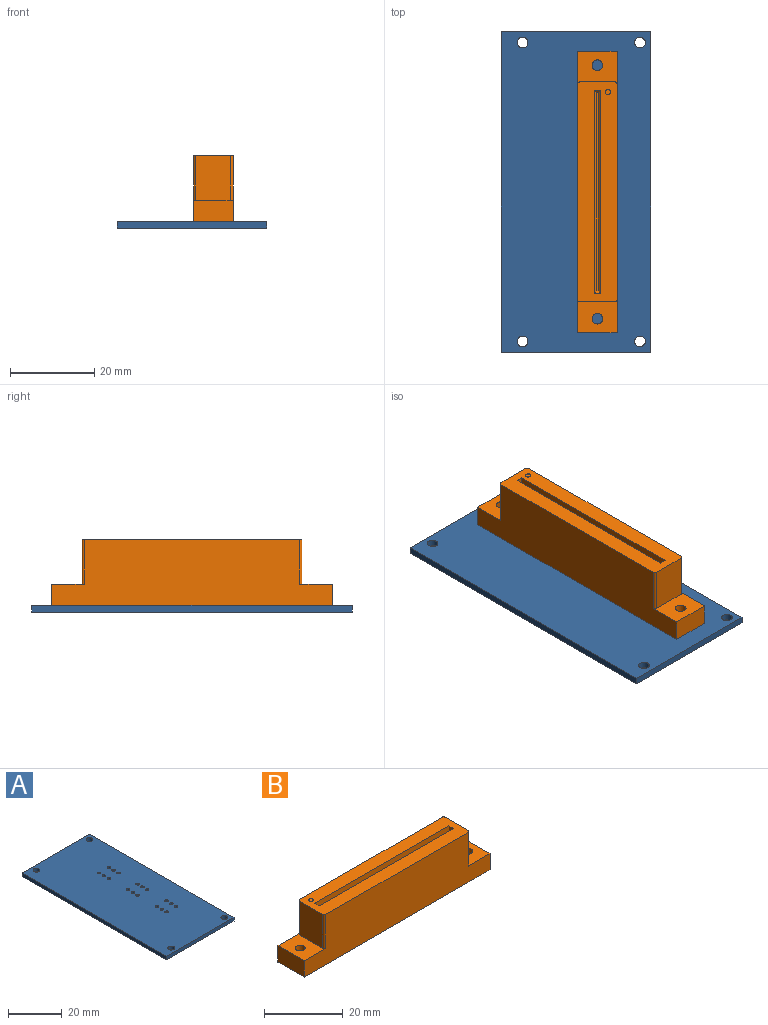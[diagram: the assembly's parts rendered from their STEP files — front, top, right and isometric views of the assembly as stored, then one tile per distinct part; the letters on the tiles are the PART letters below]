
ASSEMBLY  parts=2 mates=1
PART A: 28 faces, bbox 35.6x76.2x1.6 mm
  f0: plane 35.56x1.6mm, normal (0,-1,0), area 56.9mm2, adj f1,f25,f26,f27
  f1: plane 76.2x1.6mm, normal (1,0,0), area 121.9mm2, adj f0,f2,f26,f27
  f2: plane 35.56x1.6mm, normal (0,1,0), area 56.9mm2, adj f1,f25,f26,f27
  f3: cylinder r=0.64mm len=1.6mm, axis (0,0,-1), area 6.4mm2, adj f26,f27
  f4: cylinder r=0.64mm len=1.6mm, axis (0,0,-1), area 6.4mm2, adj f26,f27
  f5: cylinder r=0.64mm len=1.6mm, axis (0,0,-1), area 6.4mm2, adj f26,f27
  f6: cylinder r=0.64mm len=1.6mm, axis (0,0,-1), area 6.4mm2, adj f26,f27
  f7: cylinder r=0.64mm len=1.6mm, axis (0,0,-1), area 6.4mm2, adj f26,f27
  f8: cylinder r=0.64mm len=1.6mm, axis (0,0,-1), area 6.4mm2, adj f26,f27
  f9: cylinder r=0.64mm len=1.6mm, axis (0,0,-1), area 6.4mm2, adj f26,f27
  f10: cylinder r=0.64mm len=1.6mm, axis (0,0,-1), area 6.4mm2, adj f26,f27
  f11: cylinder r=0.64mm len=1.6mm, axis (0,0,-1), area 6.4mm2, adj f26,f27
  f12: cylinder r=0.64mm len=1.6mm, axis (0,0,-1), area 6.4mm2, adj f26,f27
  f13: cylinder r=0.64mm len=1.6mm, axis (0,0,-1), area 6.4mm2, adj f26,f27
  f14: cylinder r=0.64mm len=1.6mm, axis (0,0,-1), area 6.4mm2, adj f26,f27
  f15: cylinder r=1.27mm len=2.54mm, axis (0,0,-1), area 12.8mm2, adj f26,f27
  f16: cylinder r=1.27mm len=2.54mm, axis (0,0,-1), area 12.8mm2, adj f26,f27
  f17: cylinder r=1.27mm len=2.54mm, axis (0,0,-1), area 12.8mm2, adj f26,f27
  f18: cylinder r=1.27mm len=2.54mm, axis (0,0,-1), area 12.8mm2, adj f26,f27
  f19: cylinder r=0.64mm len=1.6mm, axis (0,0,-1), area 6.4mm2, adj f26,f27
  f20: cylinder r=0.64mm len=1.6mm, axis (0,0,-1), area 6.4mm2, adj f26,f27
  f21: cylinder r=0.64mm len=1.6mm, axis (0,0,-1), area 6.4mm2, adj f26,f27
  f22: cylinder r=0.64mm len=1.6mm, axis (0,0,-1), area 6.4mm2, adj f26,f27
  f23: cylinder r=0.64mm len=1.6mm, axis (0,0,-1), area 6.4mm2, adj f26,f27
  f24: cylinder r=0.64mm len=1.6mm, axis (0,0,-1), area 6.4mm2, adj f26,f27
  f25: plane 76.2x1.6mm, normal (-1,0,0), area 121.9mm2, adj f0,f2,f26,f27
  f26: plane 76.2x35.56mm, normal (0,0,1), area 2666.6mm2, adj f0,f1,f2,f3,f4,f5,f6,f7
  f27: plane 76.2x35.56mm, normal (0,0,-1), area 2666.6mm2, adj f0,f1,f2,f3,f4,f5,f6,f7
PART B: 27 faces, bbox 66.9x9.4x15.6 mm
  f0: plane 52.32x9.4mm, normal (0,0,1), area 415.4mm2, adj f1,f2,f3,f4,f6,f7,f8,f9
  f1: plane 66.93x15.6mm, normal (0,1,0), area 879.8mm2, adj f0,f5,f17,f20,f21,f22,f23,f24
  f2: plane 10.52x8.38mm, normal (-1,0,0), area 88.2mm2, adj f0,f17,f18,f23
  f3: plane 66.93x15.6mm, normal (0,-1,0), area 879.8mm2, adj f0,f5,f18,f19,f21,f22,f23,f24
  f4: plane 10.52x8.38mm, normal (1,0,0), area 88.2mm2, adj f0,f19,f20,f22
  f5: plane 66.93x9.4mm, normal (0,0,-1), area 618.9mm2, adj f1,f3,f21,f24,f25,f26
  f6: plane 48.26x7.19mm, normal (0,-1,0), area 347.1mm2, adj f0,f7,f9,f12
  f7: plane 7.19x1.55mm, normal (1,0,0), area 11.1mm2, adj f0,f6,f8,f11
  f8: plane 48.26x7.19mm, normal (0,1,0), area 347.1mm2, adj f0,f7,f9,f13
  f9: plane 7.19x1.55mm, normal (-1,0,0), area 11.1mm2, adj f0,f6,f8,f14
  f10: plane 47.24x0.53mm, normal (0,0,1), area 25.2mm2, adj f11,f12,f13,f14
  f11: plane 1.55x0.51mm, normal (0.71,0,0.71), area 0.7mm2, adj f7,f10,f12,f13
  f12: plane 48.26x0.51mm, normal (0,-0.71,0.71), area 34.3mm2, adj f6,f10,f11,f14
  f13: plane 48.26x0.51mm, normal (0,0.71,0.71), area 34.3mm2, adj f8,f10,f11,f14
  f14: plane 1.55x0.51mm, normal (-0.71,0,0.71), area 0.7mm2, adj f9,f10,f12,f13
  f15: cylinder r=0.64mm len=1.27mm, axis (0,0,1), area 0.4mm2, adj f0,f16
  f16: plane 1.27x1.27mm, normal (0,0,1), area 1.3mm2, adj f15
  f17: cylinder r=0.51mm len=10.52mm, axis (0,0,1), area 8.4mm2, adj f0,f1,f2,f23
  f18: cylinder r=0.51mm len=10.52mm, axis (0,0,-1), area 8.4mm2, adj f0,f2,f3,f23
  f19: cylinder r=0.51mm len=10.52mm, axis (0,0,1), area 8.4mm2, adj f0,f3,f4,f22
  f20: cylinder r=0.51mm len=10.52mm, axis (0,0,-1), area 8.4mm2, adj f0,f1,f4,f22
  f21: plane 9.4x5.08mm, normal (1,0,0), area 47.7mm2, adj f1,f3,f5,f22
  f22: plane 9.4x7.81mm, normal (0,0,1), area 63.7mm2, adj f1,f3,f4,f19,f20,f21,f26
  f23: plane 9.4x7.81mm, normal (0,0,1), area 63.7mm2, adj f1,f2,f3,f17,f18,f24,f25
  f24: plane 9.4x5.08mm, normal (-1,0,0), area 47.7mm2, adj f1,f3,f5,f23
  f25: cylinder r=1.27mm len=5.08mm, axis (0,0,1), area 40.5mm2, adj f5,f23
  f26: cylinder r=1.27mm len=5.08mm, axis (0,0,1), area 40.5mm2, adj f5,f22
PLACE A t=(53.73,30.54,-0.8)mm
PLACE B rot(axis=(0,0,-1),90deg) t=(36.33,42.48,0.8)mm
MATE fastened B.f5 <-> A.f26  axis (0,0,-1) through (41.03,68.64,0.8)mm
